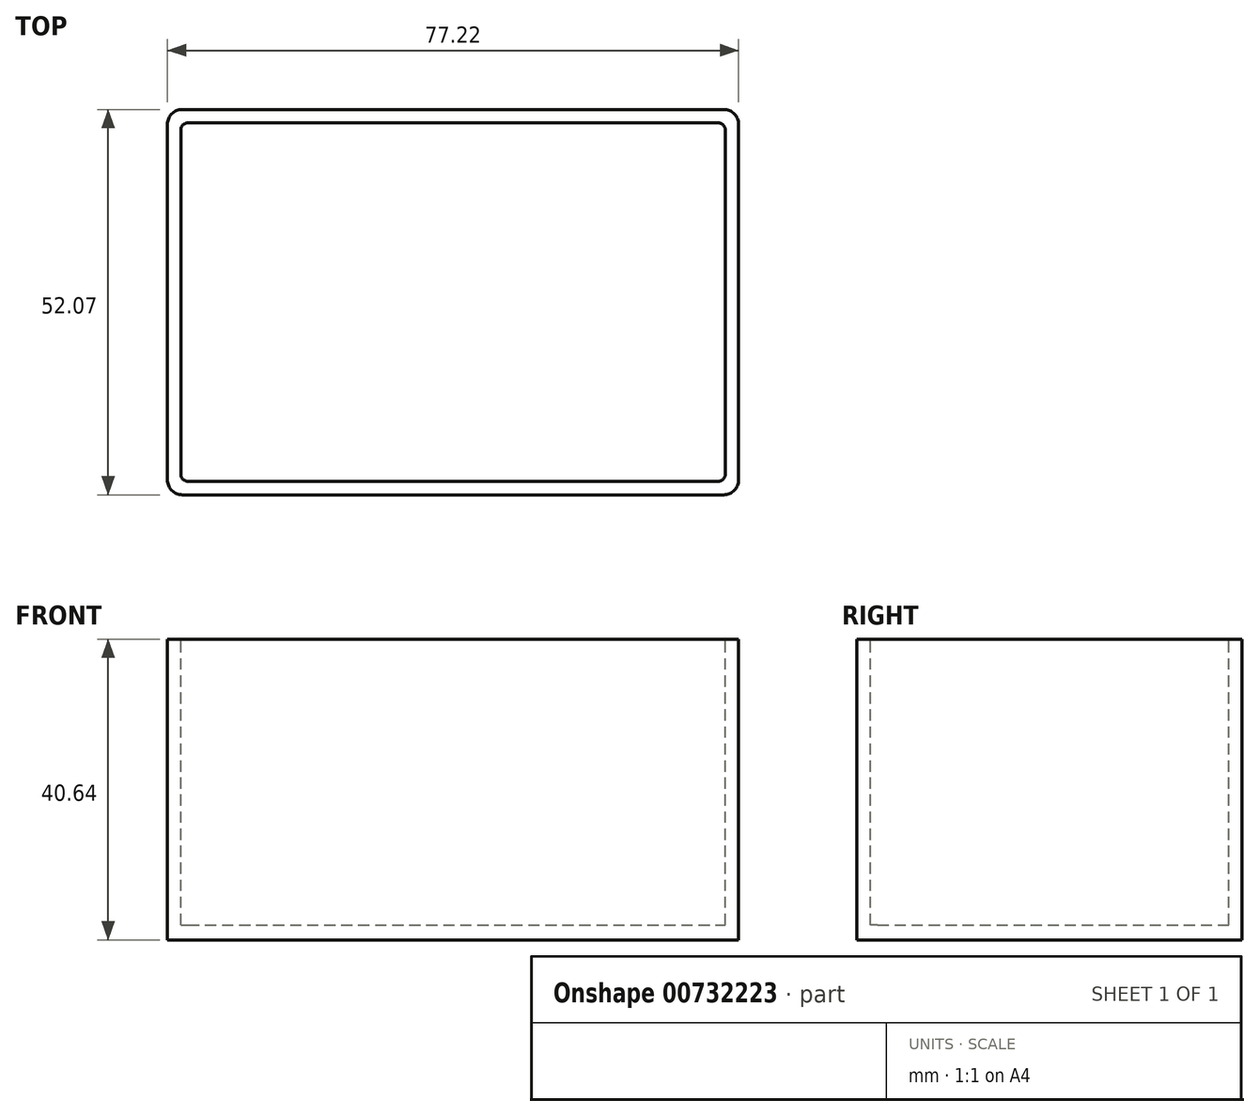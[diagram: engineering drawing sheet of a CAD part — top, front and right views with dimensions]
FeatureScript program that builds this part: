
annotation { "Feature Type Name" : "Feature", "Feature Type Description" : "" }
export const myFeature = defineFeature(function(context is Context, id is Id, definition is map)
    precondition{}
    {
        {
            var Q0;
            Q0=qCreatedBy(makeId("Top.planeOp"),FACE);
            var sketch = newSketch(context, id + "F0", { "sketchPlane" : qUnion([Q0])});
            skLineSegment(sketch, "E0.bottom", {"start": v(2, 0) * mm, "end": v(75.22, 0) * mm});
            skLineSegment(sketch, "E0.top", {"start": v(2, 52.07) * mm, "end": v(75.22, 52.07) * mm});
            skLineSegment(sketch, "E0.left", {"start": v(0, 2) * mm, "end": v(0, 50.07) * mm});
            skLineSegment(sketch, "E0.right", {"start": v(77.22, 2) * mm, "end": v(77.22, 50.07) * mm});
            skPoint(sketch, "E1.visualSharp", {"position": v(0, 52.07) * mm});
            skArc(sketch, "E1.filletArc", {"start": v(2, 52.07) * mm, "mid": v(0.59, 51.48) * mm, "end": v(0, 50.07) * mm});
            skPoint(sketch, "E2.visualSharp", {"position": v(77.22, 52.07) * mm});
            skArc(sketch, "E2.filletArc", {"start": v(77.22, 50.07) * mm, "mid": v(76.63, 51.48) * mm, "end": v(75.22, 52.07) * mm});
            skPoint(sketch, "E3.visualSharp", {"position": v(77.22, 0) * mm});
            skArc(sketch, "E3.filletArc", {"start": v(75.22, 0) * mm, "mid": v(76.63, 0.59) * mm, "end": v(77.22, 2) * mm});
            skPoint(sketch, "E4.visualSharp", {"position": v(0, 0) * mm});
            skArc(sketch, "E4.filletArc", {"start": v(0, 2) * mm, "mid": v(0.59, 0.59) * mm, "end": v(2, 0) * mm});
            skSolve(sketch);
        }
        {
            var Q0;
            Q0=qSketchRegion(id+"F0",true);
            var Q1;
            Q1=qSketchRegion(id+"F2",true);
            extrude(context, id + "F1", {"entities" : qUnion([Q0, Q1]), "depth" : 40.64 * mm, "offsetDistance" : 25 * mm});
        }
        {
            var Q0;
            Q0=makeQuery(id+"F1.opExtrude","CAP_FACE",FACE,{"disambiguationData":[OSD([sQuery(id+"F0.wireOp",EDGE,"E0.bottom"),sQuery(id+"F0.wireOp",EDGE,"E0.top"),sQuery(id+"F0.wireOp",EDGE,"E0.left"),sQuery(id+"F0.wireOp",EDGE,"E0.right"),sQuery(id+"F0.wireOp",EDGE,"E1.filletArc"),sQuery(id+"F0.wireOp",EDGE,"E2.filletArc"),sQuery(id+"F0.wireOp",EDGE,"E3.filletArc"),sQuery(id+"F0.wireOp",EDGE,"E4.filletArc")])],"isStart":false});
            var sketch = newSketch(context, id + "F2", { "sketchPlane" : qUnion([Q0])});
            skLineSegment(sketch, "E5.0", {"start": v(2, 52.07) * mm, "end": v(75.22, 52.07) * mm});
            skLineSegment(sketch, "E6.0", {"start": v(0, 2) * mm, "end": v(0, 50.07) * mm});
            skLineSegment(sketch, "E7.0", {"start": v(77.22, 2) * mm, "end": v(77.22, 50.07) * mm});
            skLineSegment(sketch, "E8.0", {"start": v(2, 0) * mm, "end": v(75.22, 0) * mm});
            skArc(sketch, "E9.0", {"start": v(2, 52.07) * mm, "mid": v(0.59, 51.48) * mm, "end": v(0, 50.07) * mm});
            skArc(sketch, "E10.0", {"start": v(77.22, 50.07) * mm, "mid": v(76.63, 51.48) * mm, "end": v(75.22, 52.07) * mm});
            skLineSegment(sketch, "E11.0", {"start": v(2.8, 50.27) * mm, "end": v(74.42, 50.27) * mm});
            skLineSegment(sketch, "E11.1", {"start": v(1.8, 2.8) * mm, "end": v(1.8, 49.27) * mm});
            skLineSegment(sketch, "E11.2", {"start": v(2.8, 1.8) * mm, "end": v(74.42, 1.8) * mm});
            skLineSegment(sketch, "E11.3", {"start": v(75.42, 2.8) * mm, "end": v(75.42, 49.27) * mm});
            skPoint(sketch, "E12.visualSharp", {"position": v(1.8, 50.27) * mm});
            skArc(sketch, "E12.filletArc", {"start": v(2.8, 50.27) * mm, "mid": v(2.1, 49.98) * mm, "end": v(1.8, 49.27) * mm});
            skPoint(sketch, "E13.visualSharp", {"position": v(1.8, 1.8) * mm});
            skArc(sketch, "E13.filletArc", {"start": v(1.8, 2.8) * mm, "mid": v(2.1, 2.1) * mm, "end": v(2.8, 1.8) * mm});
            skPoint(sketch, "E14.visualSharp", {"position": v(75.42, 1.8) * mm});
            skArc(sketch, "E14.filletArc", {"start": v(74.42, 1.8) * mm, "mid": v(75.12, 2.1) * mm, "end": v(75.42, 2.8) * mm});
            skPoint(sketch, "E15.visualSharp", {"position": v(75.42, 50.27) * mm});
            skArc(sketch, "E15.filletArc", {"start": v(75.42, 49.27) * mm, "mid": v(75.12, 49.98) * mm, "end": v(74.42, 50.27) * mm});
            skSolve(sketch);
        }
        {
            var Q0;
            Q0=qSketchRegion(id+"F2",true);
            extrude(context, id + "F3", {"entities" : qUnion([Q0]), "operationType" : NewBodyOperationType.REMOVE, "oppositeDirection" : true, "depth" : 38.6 * mm, "offsetDistance" : 25.4 * mm});
        }
    });
